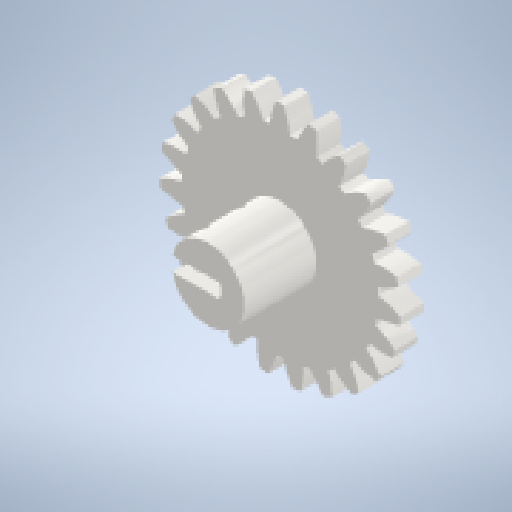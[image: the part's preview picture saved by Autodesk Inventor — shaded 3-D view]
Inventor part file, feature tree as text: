
AUTODESK INVENTOR PART (.ipt)
format: ipt  version: 2023 (Build 270158000, 158)  size: 474,624 bytes
history: native  units: mm (DEFAULTED — no unit token found)
features: extrude x4, sketch x4, projected_geometry x4, plane x3, other x3
ambient origin geometry x8: Origin, YZ Plane, XZ Plane, XY Plane, X Axis, Y Axis, Z Axis, Center Point
bodies: Solid1 (feature_tree)
feature tree (18):
  extrude  "Extrusion1"  Depth=5.0mm TaperAngle=0.0deg
  plane  "Work Plane2"
  plane  "Work Plane8"
  plane  "Work Plane9"
  other  "Spur Gear"
  extrude  "Extrusion2"  Depth=10.0mm TaperAngle=0.0deg
  extrude  "Extrusion3"  Depth=1.36591mm TaperAngle=0.0deg
  extrude  "Extrusion4"  TaperAngle=0.0deg  [1 undecoded]
  sketch  "Sketch1"  dims[d0=50.0mm d1=5.0mm d2=0.0mm]
  sketch  "Sketch2"  dims[d3=46.0mm d4=10.0mm d5=0.0mm]
  other  "Srf1"
  sketch  "Sketch3"  dims[d16=80.0mm d17=0.0mm d34=1.36591mm]
  projected_geometry  "Projected Loop1"
  sketch  "Sketch5"  dims[d39=0.0mm d41=0.0mm d43=80.0mm d46=80.0mm d47=0.0mm d48=0.0mm d49=5.5mm d50=5.0mm d51=0.0mm d52=15.0mm d53=3.0mm d54=15.0mm d55=0.0mm d56=2.0mm d57=15.0mm d58=0.0mm d59=15.0mm d60=2.5mm d61=2.5mm]
  projected_geometry  "Projected Loop3"
  projected_geometry  "Projected Loop4"
  projected_geometry  "Projected Loop5"
  other  "Pitch Diameter"
note: 1 required parameter value undecoded (feature->parameter linkage not recoverable at this tier; creation-order binding heuristic only, values carry confidence <= 0.55)
